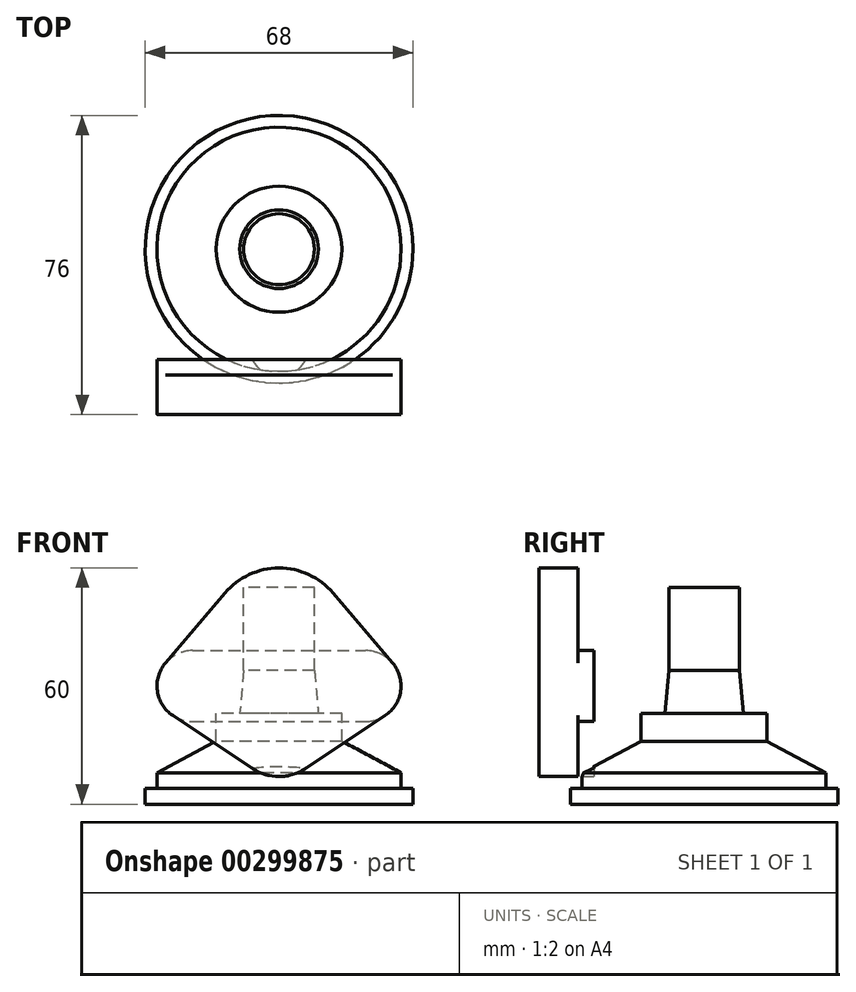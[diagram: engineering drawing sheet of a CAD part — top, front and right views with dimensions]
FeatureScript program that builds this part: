
annotation { "Feature Type Name" : "Feature", "Feature Type Description" : "" }
export const myFeature = defineFeature(function(context is Context, id is Id, definition is map)
    precondition{}
    {
        {
            var Q0;
            Q0=qCreatedBy(makeId("Front.planeOp"),FACE);
            var sketch = newSketch(context, id + "F0", { "sketchPlane" : qUnion([Q0])});
            skLineSegment(sketch, "E0", {"start": v(0, 0) * mm, "end": v(0, 58.69) * mm, "construction": true});
            skLineSegment(sketch, "E1", {"start": v(34, 0) * mm, "end": v(34, 4) * mm});
            skLineSegment(sketch, "E2", {"start": v(34, 4) * mm, "end": v(31, 4) * mm});
            skLineSegment(sketch, "E3", {"start": v(31, 4) * mm, "end": v(31, 8) * mm});
            skLineSegment(sketch, "E4", {"start": v(31, 8) * mm, "end": v(16, 16) * mm});
            skLineSegment(sketch, "E5", {"start": v(16, 16) * mm, "end": v(16, 23) * mm});
            skLineSegment(sketch, "E6", {"start": v(16, 23) * mm, "end": v(10, 23) * mm});
            skLineSegment(sketch, "E7", {"start": v(9, 34) * mm, "end": v(9, 55) * mm});
            skLineSegment(sketch, "E8", {"start": v(9, 55) * mm, "end": v(0, 55) * mm});
            skLineSegment(sketch, "E9", {"start": v(0, 55) * mm, "end": v(0, 0) * mm});
            skLineSegment(sketch, "E10", {"start": v(9, 34) * mm, "end": v(9, 34) * mm});
            skLineSegment(sketch, "E11", {"start": v(9, 34) * mm, "end": v(10, 23) * mm});
            skLineSegment(sketch, "E12", {"start": v(0, 0) * mm, "end": v(34, 0) * mm});
            skSolve(sketch);
        }
        {
            var Q0;
            Q0=makeQuery(id+"F0.imprint","IMPRINT",FACE,{"disambiguationData":[TD([[makeQuery(id+"F0.imprint","IMPRINT",EDGE,{"derivedFrom":sQuery(id+"F0.wireOp",EDGE,"E1")}),1.0]])]});
            var Q1;
            Q1=sQuery(id+"F0.wireOp",EDGE,"E9");
            revolve(context, id + "F1", {"entities" : qUnion([Q0]), "axis" : qUnion([Q1]), "revolveType" : RevolveType.FULL});
        }
        {
            var Q0;
            Q0=qCreatedBy(makeId("Front.planeOp"),FACE);
            cPlane(context, id + "F2", {"entities" : qUnion([Q0]), "cplaneType" : CPlaneType.OFFSET, "offset" : 42 * mm, "width" : 150 * mm, "height" : 150 * mm});
        }
        {
            var Q0;
            Q0=qCreatedBy(id+"F2.planeOp",FACE);
            var sketch = newSketch(context, id + "F3", { "sketchPlane" : qUnion([Q0])});
            skLineSegment(sketch, "E13", {"start": v(-71.3, 30) * mm, "end": v(51.88, 30) * mm, "construction": true});
            skLineSegment(sketch, "E14", {"start": v(0, 73.23) * mm, "end": v(0, -35.62) * mm, "construction": true});
            skArc(sketch, "E15", {"start": v(31, 30) * mm, "mid": v(30.45, 33.1) * mm, "end": v(28.86, 35.83) * mm});
            skArc(sketch, "E16", {"start": v(13.72, 53.65) * mm, "mid": v(7.56, 58.34) * mm, "end": v(0, 60) * mm});
            skLineSegment(sketch, "E17", {"start": v(13.72, 53.65) * mm, "end": v(28.86, 35.83) * mm});
            skArc(sketch, "E18", {"start": v(0, 7) * mm, "mid": v(3.47, 7.51) * mm, "end": v(6.64, 9) * mm});
            skArc(sketch, "E19", {"start": v(26.98, 22.5) * mm, "mid": v(29.93, 25.75) * mm, "end": v(31, 30) * mm});
            skLineSegment(sketch, "E20", {"start": v(26.98, 22.5) * mm, "end": v(6.64, 9) * mm});
            skArc(sketch, "E21.MirrorCS", {"start": v(-26.98, 22.5) * mm, "mid": v(-29.93, 25.75) * mm, "end": v(-31, 30) * mm});
            skLineSegment(sketch, "E22.MirrorCS", {"start": v(-13.72, 53.65) * mm, "end": v(-28.86, 35.83) * mm});
            skLineSegment(sketch, "E23.MirrorCS", {"start": v(-26.98, 22.5) * mm, "end": v(-6.64, 9) * mm});
            skArc(sketch, "E24.MirrorCS", {"start": v(0, 7) * mm, "mid": v(-3.47, 7.51) * mm, "end": v(-6.64, 9) * mm});
            skArc(sketch, "E25.MirrorCS", {"start": v(-13.72, 53.65) * mm, "mid": v(-7.56, 58.34) * mm, "end": v(0, 60) * mm});
            skArc(sketch, "E26.MirrorCS", {"start": v(-31, 30) * mm, "mid": v(-30.45, 33.1) * mm, "end": v(-28.86, 35.83) * mm});
            skSolve(sketch);
        }
        {
            var Q0;
            Q0=makeQuery(id+"F3.imprint","IMPRINT",FACE,{"disambiguationData":[TD([[makeQuery(id+"F3.imprint","IMPRINT",EDGE,{"derivedFrom":sQuery(id+"F3.wireOp",EDGE,"E15")}),1.0]])]});
            extrude(context, id + "F4", {"entities" : qUnion([Q0]), "oppositeDirection" : true, "depth" : 14 * mm});
        }
        {
            var Q0;
            Q0=makeQuery(id+"F4.opExtrude","CAP_FACE",FACE,{"disambiguationData":[OSD([sQuery(id+"F3.wireOp",EDGE,"E15"),sQuery(id+"F3.wireOp",EDGE,"E16"),sQuery(id+"F3.wireOp",EDGE,"E17"),sQuery(id+"F3.wireOp",EDGE,"E18"),sQuery(id+"F3.wireOp",EDGE,"E19"),sQuery(id+"F3.wireOp",EDGE,"E20"),sQuery(id+"F3.wireOp",EDGE,"E21.MirrorCS"),sQuery(id+"F3.wireOp",EDGE,"E22.MirrorCS"),sQuery(id+"F3.wireOp",EDGE,"E23.MirrorCS"),sQuery(id+"F3.wireOp",EDGE,"E24.MirrorCS"),sQuery(id+"F3.wireOp",EDGE,"E25.MirrorCS"),sQuery(id+"F3.wireOp",EDGE,"E26.MirrorCS")])],"isStart":false});
            var sketch = newSketch(context, id + "F5", { "sketchPlane" : qUnion([Q0])});
            skArc(sketch, "E27", {"start": v(-22, 39) * mm, "mid": v(-31, 30) * mm, "end": v(-22, 21) * mm});
            skArc(sketch, "E28", {"start": v(22, 21) * mm, "mid": v(31, 30) * mm, "end": v(22, 39) * mm});
            skLineSegment(sketch, "E29", {"start": v(22, 39) * mm, "end": v(-22, 39) * mm});
            skLineSegment(sketch, "E30", {"start": v(22, 21) * mm, "end": v(-22, 21) * mm});
            skArc(sketch, "E31.0.0", {"start": v(26.98, 22.5) * mm, "mid": v(30.91, 28.74) * mm, "end": v(28.86, 35.83) * mm});
            skLineSegment(sketch, "E31.0.1", {"start": v(28.86, 35.83) * mm, "end": v(13.72, 53.65) * mm});
            skArc(sketch, "E31.0.2", {"start": v(13.72, 53.65) * mm, "mid": v(0, 60) * mm, "end": v(-13.72, 53.65) * mm});
            skLineSegment(sketch, "E31.0.3", {"start": v(-13.72, 53.65) * mm, "end": v(-28.86, 35.83) * mm});
            skArc(sketch, "E31.0.4", {"start": v(-28.86, 35.83) * mm, "mid": v(-30.91, 28.74) * mm, "end": v(-26.98, 22.5) * mm});
            skLineSegment(sketch, "E31.0.5", {"start": v(-26.98, 22.5) * mm, "end": v(-6.64, 9) * mm});
            skArc(sketch, "E31.0.6", {"start": v(-6.64, 9) * mm, "mid": v(0, 7) * mm, "end": v(6.64, 9) * mm});
            skLineSegment(sketch, "E31.0.7", {"start": v(6.64, 9) * mm, "end": v(26.98, 22.5) * mm});
            skSolve(sketch);
        }
        {
            var Q0;
            {var subQ0=sQuery(id+"F5.wireOp",EDGE,"E30");Q0=makeQuery(id+"F5.imprint","IMPRINT",FACE,{"disambiguationData":[TD([[makeQuery(id+"F5.imprint","IMPRINT",EDGE,{"derivedFrom":subQ0}),1.0]])]});}
            var Q1;
            {var subQ1=sQuery(id+"F5.wireOp",EDGE,"E29");Q1=makeQuery(id+"F5.imprint","IMPRINT",FACE,{"disambiguationData":[TD([[makeQuery(id+"F5.imprint","IMPRINT",EDGE,{"derivedFrom":subQ1}),-1.0]])]});}
            extrude(context, id + "F6", {"entities" : qUnion([Q0, Q1]), "operationType" : NewBodyOperationType.REMOVE, "oppositeDirection" : true, "depth" : 4 * mm});
        }
    });
